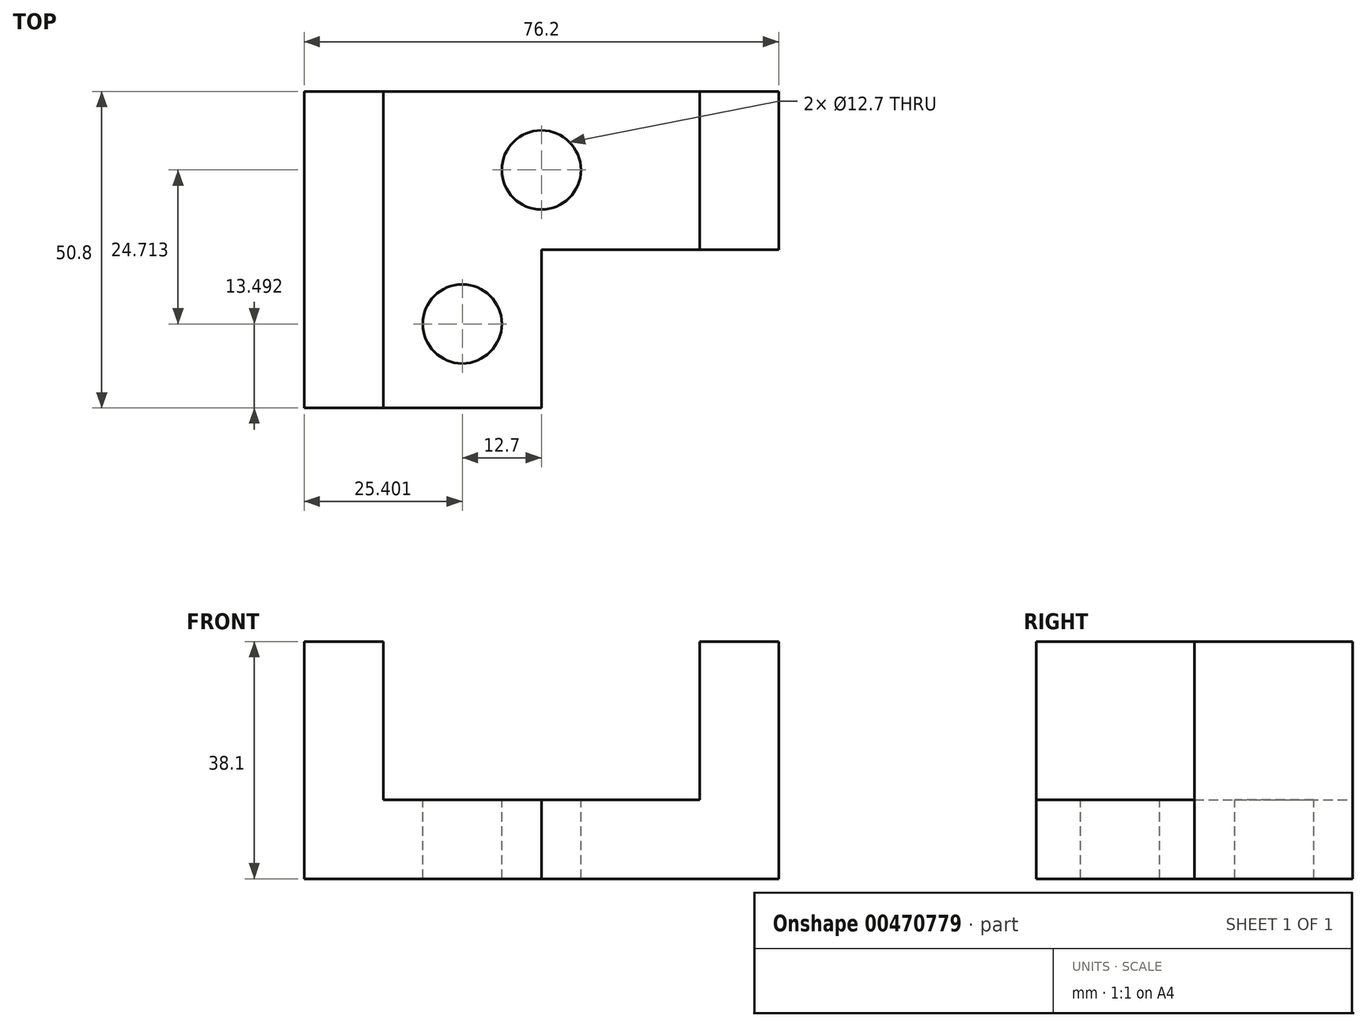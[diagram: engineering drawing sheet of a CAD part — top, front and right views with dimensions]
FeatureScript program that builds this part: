
annotation { "Feature Type Name" : "Feature", "Feature Type Description" : "" }
export const myFeature = defineFeature(function(context is Context, id is Id, definition is map)
    precondition{}
    {
        {
            var Q0;
            Q0=qCreatedBy(makeId("Front.planeOp"),FACE);
            var sketch = newSketch(context, id + "F0", { "sketchPlane" : qUnion([Q0])});
            skLineSegment(sketch, "E0.bottom", {"start": v(42.11, 6.35) * mm, "end": v(-34.09, 6.35) * mm});
            skLineSegment(sketch, "E0.top", {"start": v(42.11, -6.35) * mm, "end": v(-34.09, -6.35) * mm});
            skLineSegment(sketch, "E0.left", {"start": v(42.11, 6.35) * mm, "end": v(42.11, -6.35) * mm});
            skLineSegment(sketch, "E0.right", {"start": v(-34.09, 6.35) * mm, "end": v(-34.09, -6.35) * mm});
            skPoint(sketch, "E0.middle", {"position": v(4.01, 0) * mm});
            skSolve(sketch);
        }
        {
            var Q0;
            Q0=makeQuery(id+"F0.imprint","IMPRINT",FACE,{"disambiguationData":[TD([[makeQuery(id+"F0.imprint","IMPRINT",EDGE,{"derivedFrom":sQuery(id+"F0.wireOp",EDGE,"E0.bottom")}),1.0]])]});
            extrude(context, id + "F1", {"entities" : qUnion([Q0]), "depth" : 25.4 * mm});
        }
        {
            var Q0;
            Q0=makeQuery(id+"F1.opExtrude","CAP_FACE",FACE,{"disambiguationData":[OSD([sQuery(id+"F0.wireOp",EDGE,"E0.bottom"),sQuery(id+"F0.wireOp",EDGE,"E0.top"),sQuery(id+"F0.wireOp",EDGE,"E0.left"),sQuery(id+"F0.wireOp",EDGE,"E0.right")])],"isStart":false});
            extrude(context, id + "F2", {"entities" : qUnion([Q0]), "operationType" : NewBodyOperationType.REMOVE, "oppositeDirection" : true, "depth" : 50.8 * mm});
        }
        {
            var Q0;
            Q0 = qSketchRegion(id + "F0", true);
            extrude(context, id + "F3", {"entities" : qUnion([Q0]), "depth" : 50.8 * mm});
        }
        {
            var Q0;
            Q0=makeQuery(id+"F3.opExtrude","CAP_FACE",FACE,{"disambiguationData":[OSD([sQuery(id+"F0.wireOp",EDGE,"E0.bottom"),sQuery(id+"F0.wireOp",EDGE,"E0.top"),sQuery(id+"F0.wireOp",EDGE,"E0.left"),sQuery(id+"F0.wireOp",EDGE,"E0.right")])],"isStart":false});
            var sketch = newSketch(context, id + "F4", { "sketchPlane" : qUnion([Q0])});
            skLineSegment(sketch, "E1.bottom", {"start": v(42.11, 6.35) * mm, "end": v(4.01, 6.35) * mm});
            skLineSegment(sketch, "E1.top", {"start": v(42.11, -6.35) * mm, "end": v(4.01, -6.35) * mm});
            skLineSegment(sketch, "E1.left", {"start": v(42.11, 6.35) * mm, "end": v(42.11, -6.35) * mm});
            skLineSegment(sketch, "E1.right", {"start": v(4.01, 6.35) * mm, "end": v(4.01, -6.35) * mm});
            skSolve(sketch);
        }
        {
            var Q0;
            Q0=makeQuery(id+"F4.imprint","IMPRINT",FACE,{"disambiguationData":[TD([[makeQuery(id+"F4.imprint","IMPRINT",EDGE,{"derivedFrom":sQuery(id+"F4.wireOp",EDGE,"E1.bottom")}),1.0]])]});
            extrude(context, id + "F5", {"entities" : qUnion([Q0]), "operationType" : NewBodyOperationType.REMOVE, "oppositeDirection" : true, "depth" : 25.4 * mm});
        }
        {
            var Q0;
            Q0=makeQuery(id+"F3.opExtrude","SWEPT_FACE",FACE,{"disambiguationData":[OSD([sQuery(id+"F0.wireOp",EDGE,"E0.bottom")])]});
            var sketch = newSketch(context, id + "F6", { "sketchPlane" : qUnion([Q0])});
            skLineSegment(sketch, "E2.bottom", {"start": v(42.11, -25.4) * mm, "end": v(29.41, -25.4) * mm});
            skLineSegment(sketch, "E2.top", {"start": v(42.11, 0) * mm, "end": v(29.41, 0) * mm});
            skLineSegment(sketch, "E2.left", {"start": v(42.11, -25.4) * mm, "end": v(42.11, 0) * mm});
            skLineSegment(sketch, "E2.right", {"start": v(29.41, -25.4) * mm, "end": v(29.41, 0) * mm});
            skSolve(sketch);
        }
        {
            var Q0;
            Q0=makeQuery(id+"F6.imprint","IMPRINT",FACE,{"disambiguationData":[TD([[makeQuery(id+"F6.imprint","IMPRINT",EDGE,{"derivedFrom":sQuery(id+"F6.wireOp",EDGE,"E2.bottom")}),-1.0]])]});
            extrude(context, id + "F7", {"entities" : qUnion([Q0]), "operationType" : NewBodyOperationType.ADD, "depth" : 25.4 * mm});
        }
        {
            var Q0;
            Q0=makeQuery(id+"F3.opExtrude","SWEPT_FACE",FACE,{"disambiguationData":[OSD([sQuery(id+"F0.wireOp",EDGE,"E0.bottom")])]});
            var sketch = newSketch(context, id + "F8", { "sketchPlane" : qUnion([Q0])});
            skLineSegment(sketch, "E3.bottom", {"start": v(-34.09, -50.8) * mm, "end": v(-21.39, -50.8) * mm});
            skLineSegment(sketch, "E3.top", {"start": v(-34.09, 0) * mm, "end": v(-21.39, 0) * mm});
            skLineSegment(sketch, "E3.left", {"start": v(-34.09, -50.8) * mm, "end": v(-34.09, 0) * mm});
            skLineSegment(sketch, "E3.right", {"start": v(-21.39, -50.8) * mm, "end": v(-21.39, 0) * mm});
            skSolve(sketch);
        }
        {
            var Q0;
            Q0=makeQuery(id+"F8.imprint","IMPRINT",FACE,{"disambiguationData":[TD([[makeQuery(id+"F8.imprint","IMPRINT",EDGE,{"derivedFrom":sQuery(id+"F8.wireOp",EDGE,"E3.bottom")}),-1.0]])]});
            extrude(context, id + "F9", {"entities" : qUnion([Q0]), "operationType" : NewBodyOperationType.ADD, "depth" : 25.4 * mm});
        }
        {
            var Q0;
            Q0=makeQuery(id+"F3.opExtrude","SWEPT_FACE",FACE,{"disambiguationData":[OSD([sQuery(id+"F0.wireOp",EDGE,"E0.bottom")])]});
            var sketch = newSketch(context, id + "F10", { "sketchPlane" : qUnion([Q0])});
            skCircle(sketch, "E4", {"center": v(-8.69, -37.3) * mm, "radius": 6.35 * mm});
            skSolve(sketch);
        }
        {
            var Q0;
            Q0=makeQuery(id+"F10.imprint","IMPRINT",FACE,{"disambiguationData":[TD([[makeQuery(id+"F10.imprint","IMPRINT",EDGE,{"derivedFrom":sQuery(id+"F10.wireOp",EDGE,"E4")}),1.0]])]});
            extrude(context, id + "F11", {"entities" : qUnion([Q0]), "operationType" : NewBodyOperationType.REMOVE, "oppositeDirection" : true, "depth" : 25.4 * mm});
        }
        {
            var Q0;
            Q0=makeQuery(id+"F3.opExtrude","SWEPT_FACE",FACE,{"disambiguationData":[OSD([sQuery(id+"F0.wireOp",EDGE,"E0.bottom")])]});
            var sketch = newSketch(context, id + "F12", { "sketchPlane" : qUnion([Q0])});
            skCircle(sketch, "E5", {"center": v(4.01, -12.6) * mm, "radius": 6.35 * mm});
            skSolve(sketch);
        }
        {
            var Q0;
            Q0=makeQuery(id+"F12.imprint","IMPRINT",FACE,{"disambiguationData":[TD([[makeQuery(id+"F12.imprint","IMPRINT",EDGE,{"derivedFrom":sQuery(id+"F12.wireOp",EDGE,"E5")}),1.0]])]});
            extrude(context, id + "F13", {"entities" : qUnion([Q0]), "operationType" : NewBodyOperationType.REMOVE, "oppositeDirection" : true, "depth" : 25.4 * mm});
        }
    });
